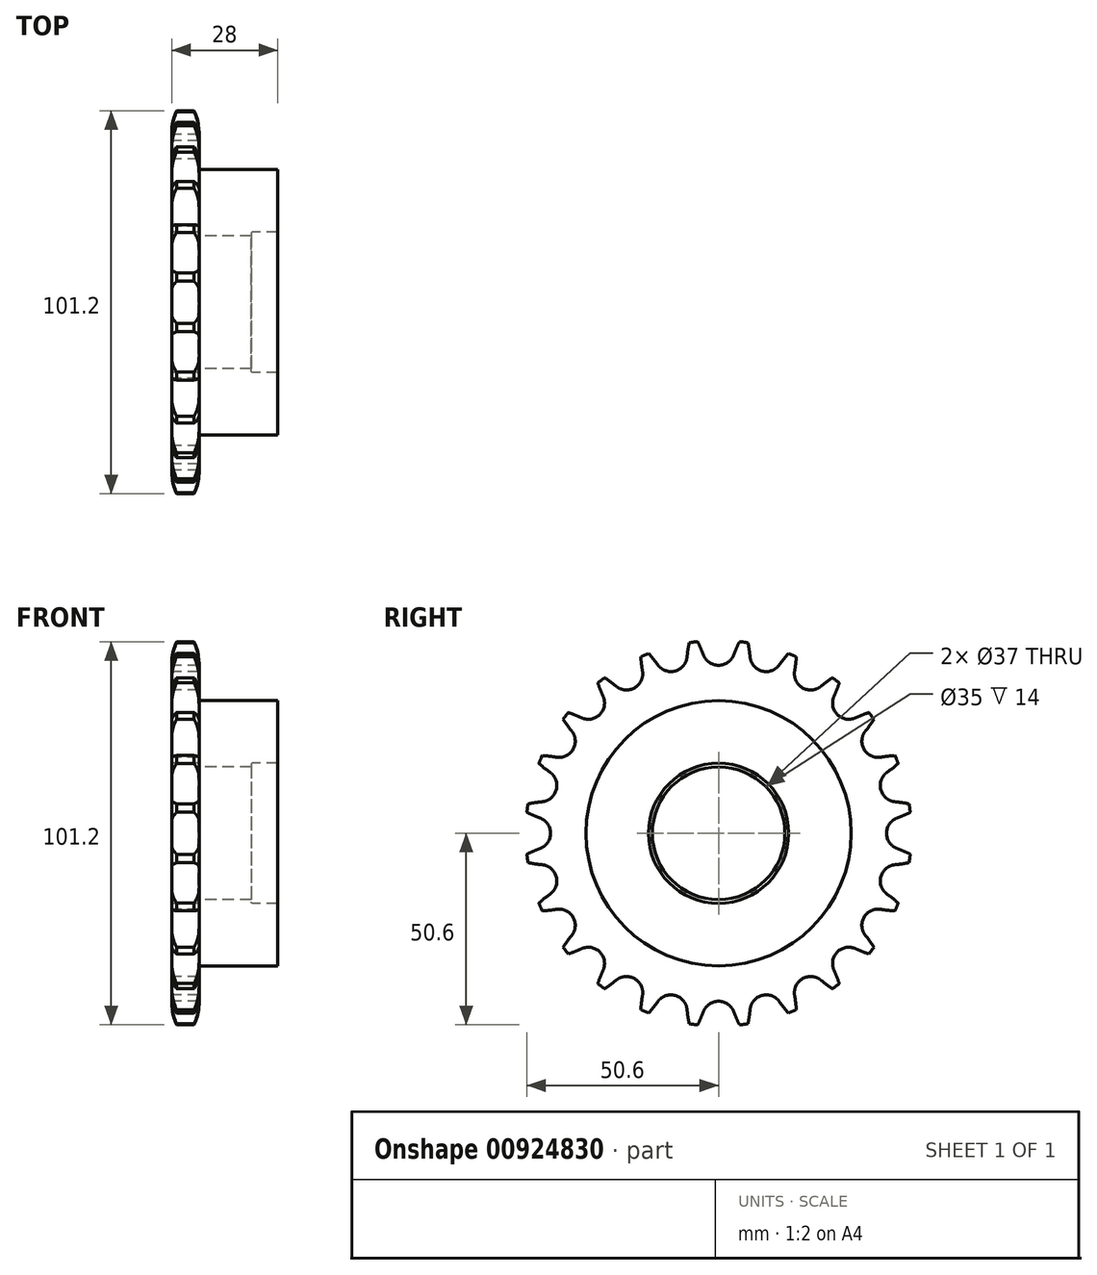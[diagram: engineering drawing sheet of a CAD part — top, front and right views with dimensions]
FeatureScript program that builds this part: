
annotation { "Feature Type Name" : "Feature", "Feature Type Description" : "" }
export const myFeature = defineFeature(function(context is Context, id is Id, definition is map)
    precondition{}
    {
        {
            var Q0;
            Q0=qCreatedBy(makeId("Front.planeOp"),FACE);
            var sketch = newSketch(context, id + "F0", { "sketchPlane" : qUnion([Q0])});
            skLineSegment(sketch, "E0", {"start": v(0, 0) * mm, "end": v(28, 0) * mm, "construction": true});
            skLineSegment(sketch, "E1", {"start": v(28, 18.5) * mm, "end": v(28, 35) * mm});
            skLineSegment(sketch, "E2", {"start": v(28, 35) * mm, "end": v(7.2, 35) * mm});
            skLineSegment(sketch, "E3", {"start": v(7.2, 35) * mm, "end": v(7.2, 45.23) * mm});
            skLineSegment(sketch, "E4", {"start": v(5.9, 50.9) * mm, "end": v(1.3, 50.9) * mm});
            skLineSegment(sketch, "E5", {"start": v(0, 45.23) * mm, "end": v(0, 18.5) * mm});
            skArc(sketch, "E6", {"start": v(1.3, 50.9) * mm, "mid": v(0.33, 48.14) * mm, "end": v(0, 45.23) * mm});
            skLineSegment(sketch, "E7", {"start": v(3.6, 50.9) * mm, "end": v(3.6, 0) * mm, "construction": true});
            skArc(sketch, "E8.MirrorCS", {"start": v(5.9, 50.9) * mm, "mid": v(6.87, 48.14) * mm, "end": v(7.2, 45.23) * mm});
            skLineSegment(sketch, "E9", {"start": v(0, 18.5) * mm, "end": v(7, 18.5) * mm});
            skLineSegment(sketch, "E10", {"start": v(7, 18.5) * mm, "end": v(7, 17.5) * mm});
            skLineSegment(sketch, "E11", {"start": v(7, 17.5) * mm, "end": v(21, 17.5) * mm});
            skLineSegment(sketch, "E12", {"start": v(21, 17.5) * mm, "end": v(21, 18.5) * mm});
            skLineSegment(sketch, "E13", {"start": v(21, 18.5) * mm, "end": v(28, 18.5) * mm});
            skSolve(sketch);
        }
        {
            var Q0;
            Q0 = qSketchRegion(id + "F0", true);
            var Q1;
            Q1=sQuery(id+"F0.wireOp",EDGE,"E0");
            revolve(context, id + "F1", {"surfaceOperationType" : NewSurfaceOperationType.NEW, "entities" : qUnion([Q0]), "axis" : qUnion([Q1]), "revolveType" : RevolveType.FULL});
        }
        {
            var Q0;
            Q0=makeQuery(id+"F1.opRevolve","SWEPT_EDGE",EDGE,{"disambiguationData":[OSD([sQuery(id+"F0.wireOp",EDGE,"E12"),sQuery(id+"F0.wireOp",EDGE,"E13")])]});
            var Q1;
            Q1=makeQuery(id+"F1.opRevolve","SWEPT_EDGE",EDGE,{"disambiguationData":[OSD([sQuery(id+"F0.wireOp",EDGE,"E9"),sQuery(id+"F0.wireOp",EDGE,"E10")])]});
            fillet(context, id + "F2", {"entities" : qUnion([Q0, Q1]), "radius" : 0.3 * mm, "tangentPropagation" : true, "allowEdgeOverflow" : false});
        }
        {
            var Q0;
            Q0=qCreatedBy(makeId("Right.planeOp"),FACE);
            var sketch = newSketch(context, id + "F3", { "sketchPlane" : qUnion([Q0])});
            skCircle(sketch, "E14", {"center": v(0, 0) * mm, "radius": 48.65 * mm, "construction": true});
            skCircle(sketch, "E15", {"center": v(-12.6, 46.99) * mm, "radius": 4.25 * mm, "construction": true});
            skCircle(sketch, "E16.MirrorC", {"center": v(0, 48.65) * mm, "radius": 4.25 * mm, "construction": true});
            skLineSegment(sketch, "E17", {"start": v(-12.6, 46.99) * mm, "end": v(0, 0) * mm, "construction": true});
            skLineSegment(sketch, "E18", {"start": v(-32.23, 36.91) * mm, "end": v(0, 48.65) * mm, "construction": true});
            skLineSegment(sketch, "E19.MirrorCS", {"start": v(32.23, 36.91) * mm, "end": v(0, 48.65) * mm, "construction": true});
            skCircle(sketch, "E20", {"center": v(0, 0) * mm, "radius": 52.9 * mm, "construction": true});
            skArc(sketch, "E21", {"start": v(-4.04, 47.17) * mm, "mid": v(0, 44.35) * mm, "end": v(4.04, 47.17) * mm});
            skArc(sketch, "E22", {"start": v(4.04, 47.17) * mm, "mid": v(5.18, 49.9) * mm, "end": v(6.59, 52.49) * mm});
            skArc(sketch, "E23.MirrorCS", {"start": v(-4.04, 47.17) * mm, "mid": v(-5.18, 49.9) * mm, "end": v(-6.59, 52.49) * mm});
            skArc(sketch, "E24", {"start": v(6.59, 52.49) * mm, "mid": v(0, 52.9) * mm, "end": v(-6.59, 52.49) * mm});
            skSolve(sketch);
        }
        {
            var Q0;
            Q0 = qSketchRegion(id + "F3", true);
            extrude(context, id + "F4", {"entities" : qUnion([Q0]), "endBound" : BoundingType.THROUGH_ALL, "depth" : 25 * mm, "offsetDistance" : 25 * mm});
        }
        {
            var Q0;
            Q0=makeQuery(id+"F4.opExtrude","SWEPT_BODY",BODY,{"disambiguationData":[OSD([sQuery(id+"F3.wireOp",EDGE,"E21"),sQuery(id+"F3.wireOp",EDGE,"E22"),sQuery(id+"F3.wireOp",EDGE,"E23.MirrorCS"),sQuery(id+"F3.wireOp",EDGE,"E24")])]});
            var Q1;
            Q1=makeQuery(id+"F1.opRevolve","SWEPT_FACE",FACE,{"disambiguationData":[OSD([sQuery(id+"F0.wireOp",EDGE,"E2")])]});
            circularPattern(context, id + "F5", {"operationType" : NewBodyOperationType.REMOVE, "entities" : qUnion([Q0]), "axis" : qUnion([Q1]), "angle" : 360 * degree, "instanceCount" : 24, "equalSpace" : true});
        }
    });
